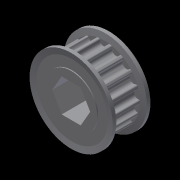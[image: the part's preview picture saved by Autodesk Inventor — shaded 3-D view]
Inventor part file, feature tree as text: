
AUTODESK INVENTOR PART (.ipt)
format: ipt  version: 2016 (Build 200138000, 138)  size: 644,096 bytes
history: native  units: in
note: dims shown in document units (in); Inventor stores cm internally (conversion verified against a paired STEP export)
features: mirror x1, other x1, imported_body x1
ambient origin geometry x8: Origin, YZ Plane, XZ Plane, XY Plane, X Axis, Y Axis, Z Axis, Center Point
bodies: Body1 (feature_tree)
feature tree (3):
  mirror  "Mirror1"
  other  "217-3225-STEP1"
  imported_body  "Base1"
